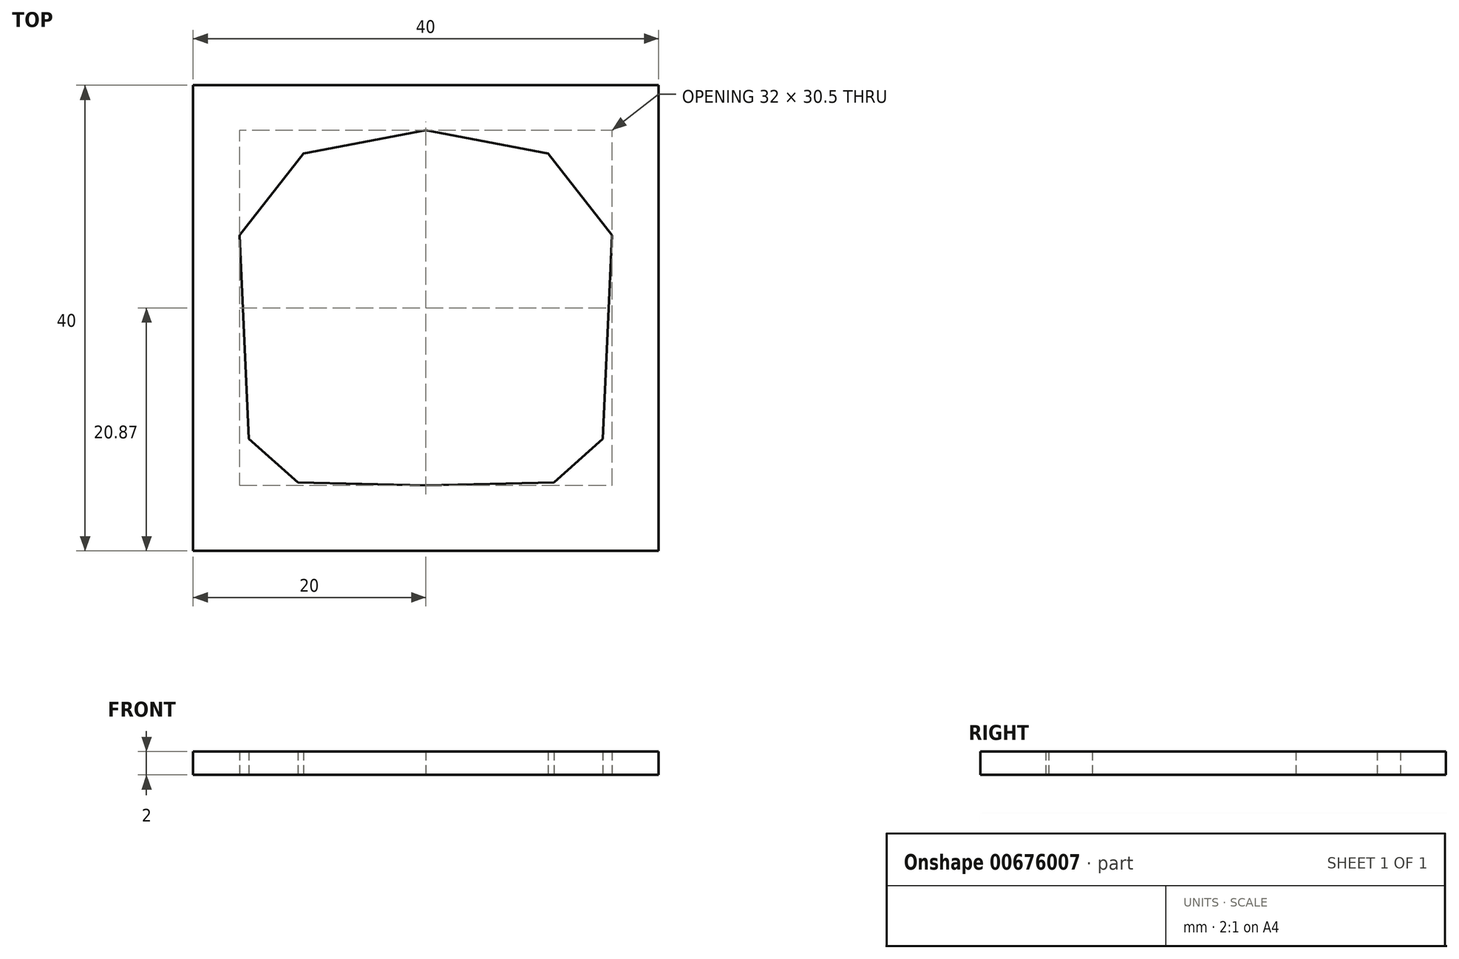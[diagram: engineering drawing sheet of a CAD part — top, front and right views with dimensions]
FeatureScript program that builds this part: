
annotation { "Feature Type Name" : "Feature", "Feature Type Description" : "" }
export const myFeature = defineFeature(function(context is Context, id is Id, definition is map)
    precondition{}
    {
        {
            var Q0;
            Q0=qCreatedBy(makeId("Top.planeOp"),FACE);
            var sketch = newSketch(context, id + "F0", { "sketchPlane" : qUnion([Q0])});
            skLineSegment(sketch, "E0", {"start": v(11, 9.27) * mm, "end": v(11, -18.55) * mm, "construction": true});
            skLineSegment(sketch, "E1", {"start": v(15.2, 11.89) * mm, "end": v(15.2, -16.1) * mm, "construction": true});
            skLineSegment(sketch, "E2", {"start": v(10.5, 35.77) * mm, "end": v(10.5, 23.15) * mm, "construction": true});
            skLineSegment(sketch, "E3", {"start": v(16, 34.98) * mm, "end": v(16, 24.29) * mm, "construction": true});
            skPoint(sketch, "E4", {"position": v(0, 30.5) * mm});
            skLineSegment(sketch, "E5", {"start": v(2.81, 0.25) * mm, "end": v(25.53, 0.25) * mm, "construction": true});
            skLineSegment(sketch, "E6", {"start": v(6.59, 4) * mm, "end": v(22.63, 4) * mm, "construction": true});
            skPoint(sketch, "E7", {"position": v(11, 0.25) * mm});
            skPoint(sketch, "E8", {"position": v(15.2, 4) * mm});
            skLineSegment(sketch, "E9", {"start": v(3.08, 21.5) * mm, "end": v(22.98, 21.5) * mm, "construction": true});
            skLineSegment(sketch, "E10", {"start": v(3.6, 28.5) * mm, "end": v(21.58, 28.5) * mm, "construction": true});
            skPoint(sketch, "E11", {"position": v(10.5, 28.5) * mm});
            skPoint(sketch, "E12", {"position": v(16, 21.5) * mm});
            skLineSegment(sketch, "E13", {"start": v(0, 30.5) * mm, "end": v(10.5, 28.5) * mm});
            skLineSegment(sketch, "E14", {"start": v(10.5, 28.5) * mm, "end": v(16, 21.5) * mm});
            skLineSegment(sketch, "E15", {"start": v(16, 21.5) * mm, "end": v(15.2, 4) * mm});
            skLineSegment(sketch, "E16", {"start": v(15.2, 4) * mm, "end": v(11, 0.25) * mm});
            skLineSegment(sketch, "E17", {"start": v(11, 0.25) * mm, "end": v(0, 0) * mm});
            skLineSegment(sketch, "E18", {"start": v(0, -5.62) * mm, "end": v(20, -5.62) * mm});
            skLineSegment(sketch, "E19", {"start": v(20, -5.62) * mm, "end": v(20, 34.38) * mm});
            skLineSegment(sketch, "E20", {"start": v(20, 34.38) * mm, "end": v(0, 34.38) * mm});
            skLineSegment(sketch, "E21.MirrorCS", {"start": v(0, 30.5) * mm, "end": v(-10.5, 28.5) * mm});
            skLineSegment(sketch, "E22.MirrorCS", {"start": v(-10.5, 28.5) * mm, "end": v(-16, 21.5) * mm});
            skLineSegment(sketch, "E23.MirrorCS", {"start": v(-16, 21.5) * mm, "end": v(-15.2, 4) * mm});
            skLineSegment(sketch, "E24.MirrorCS", {"start": v(-15.2, 4) * mm, "end": v(-11, 0.25) * mm});
            skLineSegment(sketch, "E25.MirrorCS", {"start": v(-11, 0.25) * mm, "end": v(0, 0) * mm});
            skLineSegment(sketch, "E26.MirrorCS", {"start": v(0, -5.62) * mm, "end": v(-20, -5.62) * mm});
            skLineSegment(sketch, "E27.MirrorCS", {"start": v(-20, -5.62) * mm, "end": v(-20, 34.38) * mm});
            skLineSegment(sketch, "E28.MirrorCS", {"start": v(-20, 34.38) * mm, "end": v(0, 34.38) * mm});
            skSolve(sketch);
        }
        {
            var Q0;
            Q0=makeQuery(id+"F0.imprint","IMPRINT",FACE,{"disambiguationData":[TD([[makeQuery(id+"F0.imprint","IMPRINT",EDGE,{"derivedFrom":sQuery(id+"F0.wireOp",EDGE,"E13")}),1.0]])]});
            extrude(context, id + "F1", {"entities" : qUnion([Q0]), "depth" : 2 * mm, "offsetDistance" : 25 * mm});
        }
    });
